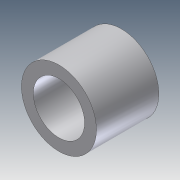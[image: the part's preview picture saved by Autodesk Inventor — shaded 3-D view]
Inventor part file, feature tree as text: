
AUTODESK INVENTOR PART (.ipt)
format: ipt  version: 2012 (Build 160160000, 160)  size: 82,432 bytes
history: native  units: in
note: dims shown in document units (in); Inventor stores cm internally (conversion verified against a paired STEP export)
features: extrude x1, sketch x1
ambient origin geometry x8: Origin, YZ Plane, XZ Plane, XY Plane, X Axis, Y Axis, Z Axis, Center Point
bodies: Solid1 (feature_tree)
feature tree (2):
  extrude  "Extrusion1"  Depth=0.257in
  sketch  "Sketch1"  dims[d0=0.375in d1=0.257in d2=0.3125in d3=0.0in]
